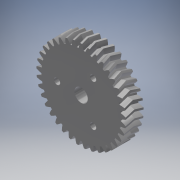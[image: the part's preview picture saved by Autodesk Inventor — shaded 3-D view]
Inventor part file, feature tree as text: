
AUTODESK INVENTOR PART (.ipt)
format: ipt  version: 2019 (Build 230136000, 136)  size: 912,384 bytes
history: native  units: mm (DEFAULTED — no unit token found)
features: sketch x4, plane x3, other x3, extrude x2, mirror x1, hole x1
ambient origin geometry x8: Origin, YZ Plane, XZ Plane, XY Plane, X Axis, Y Axis, Z Axis, Center Point
bodies: Solid1 (feature_tree)
feature tree (14):
  extrude  "Extrusion1"  Depth=5.0mm TaperAngle=0.0deg
  plane  "Work Plane2"
  plane  "Work Plane8"
  plane  "Work Plane9"
  other  "Spur Gear"
  mirror  "Mirror1"
  extrude  "Extrusion4"  Depth=10.0mm TaperAngle=0.0deg
  hole  "Hole4"  [1 undecoded]
  sketch  "Sketch1"  dims[d0=50.240958mm d1=5.0mm d2=0.0mm]
  sketch  "Sketch2"  dims[d3=47.741935mm d4=10.0mm d5=0.0mm]
  other  "Srf1"
  sketch  "Sketch6"  dims[d16=40.0mm d17=0.0mm d34=0.849079mm]
  sketch  "Sketch9"  dims[d39=0.0mm d41=0.0mm d43=40.0mm d46=40.0mm d47=0.0mm d48=0.0mm d66=7.5mm d67=5.0mm d68=0.0mm d92=27.0mm d93=30.0mm d95=360.0deg d97=3.5mm d98=6.0mm d99=6.5mm d100=6.0mm d101=14.835299mm d102=6.0mm d103=90.0deg]
  other  "Pitch Diameter"
note: 1 required parameter value undecoded (feature->parameter linkage not recoverable at this tier; creation-order binding heuristic only, values carry confidence <= 0.55)
